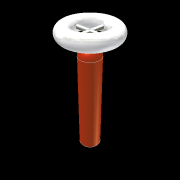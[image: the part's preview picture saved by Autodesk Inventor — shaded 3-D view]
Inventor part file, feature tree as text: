
AUTODESK INVENTOR PART (.ipt)
format: ipt  version: unknown  size: 235,008 bytes
history: native  units: in
note: dims shown in document units (in); Inventor stores cm internally (conversion verified against a paired STEP export)
features: sketch x6, extrude x4, sweep x1, fillet x1
ambient origin geometry x8: Origin, YZ Plane, XZ Plane, XY Plane, X Axis, Y Axis, Z Axis, Center Point
feature tree (12):
  extrude  "Extrusion1"  TaperAngle=0.0deg  [1 undecoded]
  sweep  "Sweep1"
  fillet  "Fillet1"  Radius=4.0in
  extrude  "Extrusion2"  [1 undecoded]
  extrude  "Extrusion3"  [1 undecoded]
  extrude  "Extrusion4"  [1 undecoded]
  sketch  "Sketch1"  dims[d0=10.0in d1=0.0in d2=0.0in]
  sketch  "Sketch2"  dims[d3=2.0in d4=0.0in d5=1.0in d6=4.0in d7=0.0in]
  sketch  "Sketch3"  dims[d8=4.0in d9=0.0in]
  sketch  "Sketch4"
  sketch  "Sketch5"
  sketch  "Sketch6"
note: 4 required parameter values undecoded (feature->parameter linkage not recoverable at this tier; creation-order binding heuristic only, values carry confidence <= 0.55)
